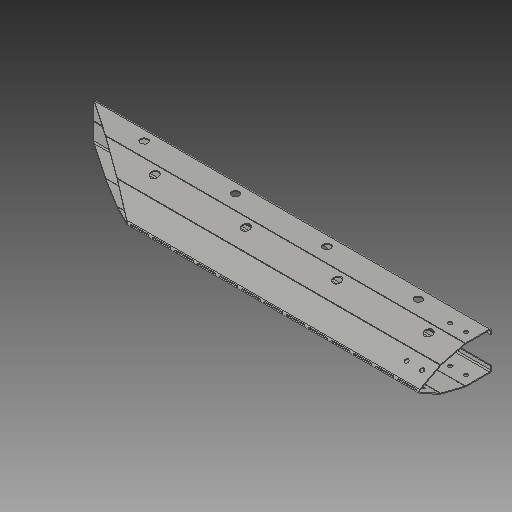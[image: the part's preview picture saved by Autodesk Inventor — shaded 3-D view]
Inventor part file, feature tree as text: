
AUTODESK INVENTOR PART (.ipt)
format: ipt  version: 2018 (Build 220112000, 112)  size: 856,064 bytes
history: native  units: mm
features: reference x24, sketch x22, other x21, hole x16, sheet_metal_op x13, plane x9, projected_geometry x7, extrude x4
ambient origin geometry x8: Origin, YZ Plane, XZ Plane, XY Plane, X Axis, Y Axis, Z Axis, Center Point
bodies: Solid1 (feature_tree)
feature tree (116):
  parser-record x4  (decoder bookkeeping rows leaked as tree rows — omitted from the tree; the rows remain in map.json)
  plane  "Work Plane1"
  sheet_metal_op  "Face1"
  plane  "Work Plane2"
  sheet_metal_op  "Face2"
  plane  "Work Plane3"
  sheet_metal_op  "Face3"
  plane  "Work Plane4"
  sheet_metal_op  "Face4"
  plane  "Work Plane5"
  sheet_metal_op  "Face5"
  plane  "Work Plane6"
  sheet_metal_op  "Face6"
  plane  "Work Plane7"
  sheet_metal_op  "Face7"
  other  "midtplan"
  extrude  "Extrusion3"  Depth=3.75mm
  extrude  "hulsæt til stifter"  Depth=3.0mm
  plane  "Work Plane11"
  sketch  "Sketch13"  dims[d18=1.5mm d19=6.0mm]
  plane  "Work Plane12"
  extrude  "balusterhul"  Depth=3.75mm
  extrude  "balusterhul skråkompensering"  Depth=3.0mm
  hole  "Hole2"  [1 undecoded]
  hole  "Hole4"  [1 undecoded]
  hole  "Hole6"  [1 undecoded]
  hole  "Hole8"  [1 undecoded]
  hole  "Hole10"  [1 undecoded]
  hole  "Hole12"  [1 undecoded]
  hole  "Hole14"  [1 undecoded]
  hole  "Hole16"  [1 undecoded]
  sketch  "Sketch1"  dims[d0=3.0mm d1=3.75mm]
  reference  "Reference1"
  reference  "Reference2"
  reference  "Reference3"
  reference  "Reference4"
  other  "Plate1"
  sketch  "Sketch2"  dims[d2=3.0mm d3=1.5mm]
  reference  "Reference5"
  reference  "Reference6"
  reference  "Reference7"
  reference  "Reference8"
  other  "Plate2"
  sheet_metal_op  "Bend1"
  sketch  "Sketch3"  dims[d4=6.0mm d5=3.75mm]
  reference  "Reference9"
  reference  "Reference10"
  reference  "Reference11"
  other  "Plate3"
  sheet_metal_op  "Bend2"
  sketch  "Sketch4"  dims[d6=3.75mm d7=3.0mm]
  reference  "Reference12"
  reference  "Reference13"
  reference  "Reference14"
  reference  "Reference15"
  other  "Plate4"
  sheet_metal_op  "Bend3"
  sketch  "Sketch5"  dims[d8=1.5mm d9=6.0mm]
  reference  "Reference16"
  reference  "Reference17"
  reference  "Reference18"
  other  "Plate5"
  sheet_metal_op  "Bend4"
  sketch  "Sketch6"  dims[d10=3.75mm d11=3.75mm]
  reference  "Reference19"
  reference  "Reference20"
  reference  "Reference21"
  other  "Plate6"
  sheet_metal_op  "Bend5"
  sketch  "Sketch7"  dims[d12=3.0mm d13=1.5mm]
  reference  "Reference22"
  reference  "Reference23"
  other  "Plate7"
  sheet_metal_op  "Bend6"
  sketch  "Sketch8"  dims[d14=6.0mm d15=3.75mm]
  reference  "Reference24"
  projected_geometry  "Projected Loop1"
  other  "huller til stifter"
  projected_geometry  "Projected Loop3"
  sketch  "Sketch12"  dims[d16=3.75mm d17=3.0mm]
  projected_geometry  "Projected Loop4"
  sketch  "Sketch14"  dims[d20=3.75mm d21=3.75mm]
  sketch  "Sketch15"  dims[d22=3.0mm d23=1.5mm]
  projected_geometry  "Projected Loop5"
  projected_geometry  "Projected Loop6"
  sketch  "Sketch16"  dims[d24=6.0mm d25=3.75mm]
  projected_geometry  "Projected Loop7"
  projected_geometry  "Projected Loop8"
  sketch  "Sketch17"  dims[d26=3.75mm d27=3.0mm]
  sketch  "Sketch18"  dims[d28=1.5mm d29=6.0mm]
  hole  "Hole1"  [1 undecoded]
  sketch  "Sketch19"  dims[d30=3.75mm d31=3.0mm]
  hole  "Hole3"  [1 undecoded]
  sketch  "Sketch20"  dims[d32=0.0mm d33=3.0mm]
  hole  "Hole5"  [1 undecoded]
  sketch  "Sketch21"  dims[d39=250.0mm d41=33.7mm]
  hole  "Hole7"  [1 undecoded]
  sketch  "Sketch22"  dims[d42=33.7mm d43=60.0mm d44=60.0mm]
  hole  "Hole9"  [1 undecoded]
  sketch  "Sketch23"  dims[d45=16.85mm d46=65.0mm]
  hole  "Hole11"  [1 undecoded]
  sketch  "Sketch24"  dims[d47=60.0mm]
  hole  "Hole13"  [1 undecoded]
  sketch  "Sketch25"  dims[d48=10.0mm d49=0.0mm d69=10.0mm d70=0.0mm d73=96.672mm d75=5.986479mm d76=180.0mm d77=26.6mm d78=25.8mm d79=40.0mm d81=302.737mm d82=10.0mm d84=10.0mm d86=90.0deg d87=113.655385mm d88=56.827692mm d89=90.0deg d90=49.0mm d91=100.0mm d92=0.0mm d95=100.0mm d96=0.0mm d97=2.046461mm d99=1.023231mm d100=90.0mm d101=30.0mm d102=30.0mm d103=342.765mm d104=342.765mm d105=30.0mm d106=342.765mm d107=10.0mm d108=3.0mm d109=0.0mm d110=8.0mm d111=6.0mm d112=61.6mm d113=140.0mm d115=73.92mm d116=10.0mm d118=10.0mm d120=3.0mm d121=0.0mm d122=13.5mm d123=6.0mm d124=4.0mm d125=2.0mm d126=90.0deg d127=8.0mm d128=0.0mm d129=13.5mm d130=6.0mm d131=4.0mm d132=2.0mm d133=90.0deg d134=8.0mm d135=0.0mm d136=13.5mm d137=6.0mm d138=4.0mm d139=2.0mm d140=90.0deg d141=8.0mm d142=0.0mm d143=13.5mm d144=6.0mm d145=4.0mm d146=2.0mm d147=90.0deg d148=8.0mm d149=0.0mm d150=13.5mm d151=6.0mm d152=4.0mm d153=2.0mm d154=90.0deg d155=8.0mm d156=0.0mm d157=13.5mm d158=6.0mm d159=4.0mm d160=2.0mm d161=90.0deg d162=8.0mm d163=0.0mm d164=13.5mm d165=6.0mm d166=4.0mm d167=2.0mm d168=90.0deg d169=8.0mm d170=0.0mm d171=13.5mm d172=6.0mm d173=4.0mm d174=2.0mm d175=90.0deg d176=8.0mm d177=0.0mm d178=1.0mm d179=1.0mm]
  hole  "Hole15"  [1 undecoded]
  other  "Cut1"
  other  "plantehuller"
  other  "bukkeperforering"
  other  "modul bund.iam"
  other  "model:1"
  other  "Definition1"
  other  "modul.iam"
  other  "modul top.iam"
note: 16 required parameter values undecoded (feature->parameter linkage not recoverable at this tier; creation-order binding heuristic only, values carry confidence <= 0.55)
note: 4 file-system paths scrubbed to <path> (originals preserved in map.json)
